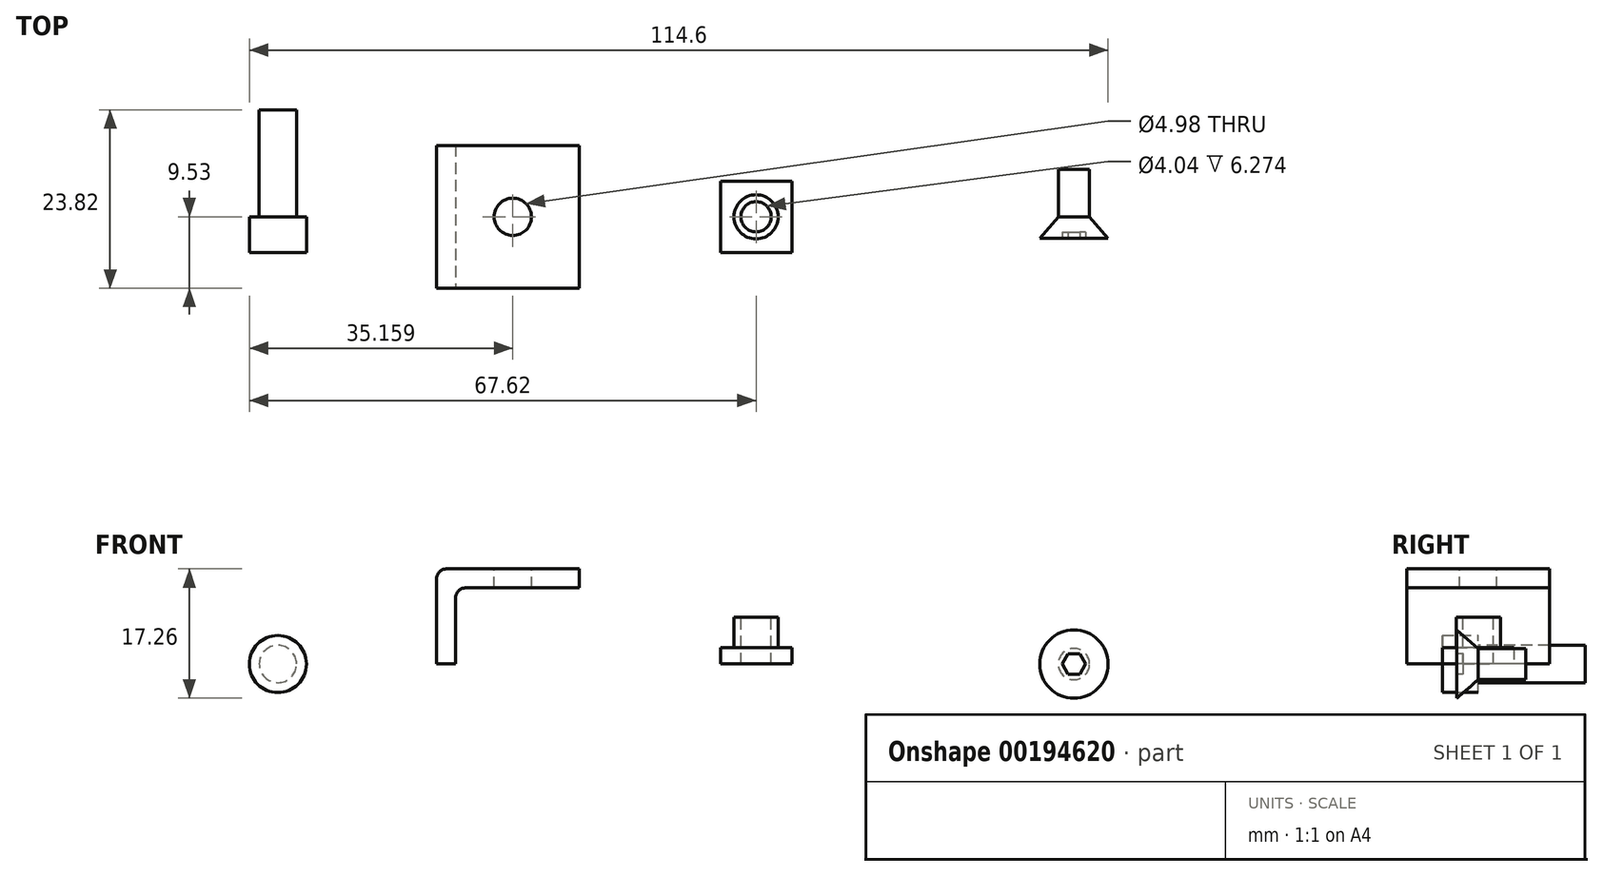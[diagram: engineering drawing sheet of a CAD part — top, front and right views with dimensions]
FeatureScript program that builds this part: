
annotation { "Feature Type Name" : "Feature", "Feature Type Description" : "" }
export const myFeature = defineFeature(function(context is Context, id is Id, definition is map)
    precondition{}
    {
        {
            var Q0;
            Q0=qCreatedBy(makeId("Top.planeOp"),FACE);
            var sketch = newSketch(context, id + "F0", { "sketchPlane" : qUnion([Q0])});
            skLineSegment(sketch, "E0.bottom", {"start": v(4.76, 4.76) * mm, "end": v(-4.76, 4.76) * mm});
            skLineSegment(sketch, "E0.top", {"start": v(4.76, -4.76) * mm, "end": v(-4.76, -4.76) * mm});
            skLineSegment(sketch, "E0.left", {"start": v(4.76, 4.76) * mm, "end": v(4.76, -4.76) * mm});
            skLineSegment(sketch, "E0.right", {"start": v(-4.76, 4.76) * mm, "end": v(-4.76, -4.76) * mm});
            skPoint(sketch, "E0.middle", {"position": v(0, 0) * mm});
            skSolve(sketch);
        }
        {
            var Q0;
            Q0=qSketchRegion(id+"F0",true);
            extrude(context, id + "F1", {"entities" : qUnion([Q0]), "depth" : 2.2 * mm});
        }
        {
            var Q0;
            Q0=makeQuery(id+"F1.opExtrude","CAP_FACE",FACE,{"disambiguationData":[OSD([sQuery(id+"F0.wireOp",EDGE,"E0.bottom"),sQuery(id+"F0.wireOp",EDGE,"E0.top"),sQuery(id+"F0.wireOp",EDGE,"E0.left"),sQuery(id+"F0.wireOp",EDGE,"E0.right")])],"isStart":false});
            var sketch = newSketch(context, id + "F2", { "sketchPlane" : qUnion([Q0])});
            skCircle(sketch, "E1", {"center": v(0, 0) * mm, "radius": 2.95 * mm});
            skSolve(sketch);
        }
        {
            var Q0;
            Q0=qSketchRegion(id+"F2",true);
            extrude(context, id + "F3", {"entities" : qUnion([Q0]), "operationType" : NewBodyOperationType.ADD, "depth" : 4.06 * mm});
        }
        {
            var Q0;
            Q0=makeQuery(id+"F3.opExtrude","CAP_FACE",FACE,{"disambiguationData":[OSD([sQuery(id+"F2.wireOp",EDGE,"E1")])],"isStart":false});
            var sketch = newSketch(context, id + "F4", { "sketchPlane" : qUnion([Q0])});
            skPoint(sketch, "E2", {"position": v(0, 0) * mm});
            skSolve(sketch);
        }
        {
            var Q0;
            Q0=sQuery(id+"F4.wireOp",VERTEX,"E2");
            var Q1;
            Q1=makeQuery(id+"F1.opExtrude","SWEPT_BODY",BODY,{"disambiguationData":[OSD([sQuery(id+"F0.wireOp",EDGE,"E0.bottom"),sQuery(id+"F0.wireOp",EDGE,"E0.top"),sQuery(id+"F0.wireOp",EDGE,"E0.left"),sQuery(id+"F0.wireOp",EDGE,"E0.right")])]});
            hole(context, id + "F5", {"style" : HoleStyle.SIMPLE, "holeDiameter" : 4.04 * mm, "endStyle" : HoleEndStyle.THROUGH, "locations" : qUnion([Q0]), "scope" : qUnion([Q1])});
        }
        {
            var Q0;
            Q0=qCreatedBy(makeId("Front.planeOp"),FACE);
            var sketch = newSketch(context, id + "F6", { "sketchPlane" : qUnion([Q0])});
            skLineSegment(sketch, "E3.bottom", {"start": v(-42.62, 0) * mm, "end": v(-23.57, 0) * mm});
            skLineSegment(sketch, "E3.top", {"start": v(-42.62, 12.7) * mm, "end": v(-23.57, 12.7) * mm});
            skLineSegment(sketch, "E3.left", {"start": v(-42.62, 0) * mm, "end": v(-42.62, 12.7) * mm});
            skLineSegment(sketch, "E3.right", {"start": v(-23.57, 0) * mm, "end": v(-23.57, 12.7) * mm});
            skSolve(sketch);
        }
        {
            var Q0;
            Q0=qSketchRegion(id+"F6",true);
            extrude(context, id + "F7", {"entities" : qUnion([Q0]), "endBound" : BoundingType.SYMMETRIC, "depth" : 19.05 * mm});
        }
        {
            var Q0;
            Q0=makeQuery(id+"F7.opExtrude","CAP_FACE",FACE,{"disambiguationData":[OSD([sQuery(id+"F6.wireOp",EDGE,"E3.bottom"),sQuery(id+"F6.wireOp",EDGE,"E3.top"),sQuery(id+"F6.wireOp",EDGE,"E3.left"),sQuery(id+"F6.wireOp",EDGE,"E3.right")])],"isStart":false});
            var sketch = newSketch(context, id + "F8", { "sketchPlane" : qUnion([Q0])});
            skLineSegment(sketch, "E4", {"start": v(-40.08, 0) * mm, "end": v(-40.08, 10.16) * mm});
            skLineSegment(sketch, "E5", {"start": v(-40.08, 10.16) * mm, "end": v(-23.57, 10.16) * mm});
            skLineSegment(sketch, "E6", {"start": v(-23.57, 10.16) * mm, "end": v(-23.57, 0) * mm});
            skLineSegment(sketch, "E7", {"start": v(-23.57, 0) * mm, "end": v(-40.08, 0) * mm});
            skSolve(sketch);
        }
        {
            var Q0;
            Q0=qSketchRegion(id+"F8",true);
            extrude(context, id + "F9", {"entities" : qUnion([Q0]), "operationType" : NewBodyOperationType.REMOVE, "endBound" : BoundingType.THROUGH_ALL, "oppositeDirection" : true, "depth" : 25.4 * mm});
        }
        {
            var Q0;
            Q0=makeQuery(id+"F7.opExtrude","SWEPT_EDGE",EDGE,{"disambiguationData":[OSD([sQuery(id+"F6.wireOp",EDGE,"E3.top"),sQuery(id+"F6.wireOp",EDGE,"E3.left")])]});
            var Q1;
            Q1=makeQuery(id+"F9.boolean.opBoolean","COPY",EDGE,{"derivedFrom":makeQuery(id+"F9.opExtrude","SWEPT_EDGE",EDGE,{"disambiguationData":[OSD([sQuery(id+"F8.wireOp",EDGE,"E4"),sQuery(id+"F8.wireOp",EDGE,"E5")])]})});
            fillet(context, id + "F10", {"entities" : qUnion([Q0, Q1]), "radius" : 1.27 * mm, "tangentPropagation" : true, "allowEdgeOverflow" : false});
        }
        {
            var Q0;
            Q0=makeQuery(id+"F7.opExtrude","SWEPT_FACE",FACE,{"disambiguationData":[OSD([sQuery(id+"F6.wireOp",EDGE,"E3.top")])]});
            var sketch = newSketch(context, id + "F11", { "sketchPlane" : qUnion([Q0])});
            skPoint(sketch, "E8", {"position": v(-32.46, 0) * mm});
            skLineSegment(sketch, "E9", {"start": v(-32.46, 9.52) * mm, "end": v(-32.46, 0) * mm, "construction": true});
            skLineSegment(sketch, "E10", {"start": v(-32.46, -9.52) * mm, "end": v(-32.46, 0) * mm, "construction": true});
            skLineSegment(sketch, "E11", {"start": v(-32.46, 0) * mm, "end": v(-23.57, 0) * mm, "construction": true});
            skLineSegment(sketch, "E12", {"start": v(-42.62, 0) * mm, "end": v(-32.46, 0) * mm, "construction": true});
            skSolve(sketch);
        }
        {
            var Q0;
            Q0=sQuery(id+"F11.wireOp",VERTEX,"E8");
            var Q1;
            Q1=makeQuery(id+"F7.opExtrude","SWEPT_BODY",BODY,{"disambiguationData":[OSD([sQuery(id+"F6.wireOp",EDGE,"E3.bottom"),sQuery(id+"F6.wireOp",EDGE,"E3.top"),sQuery(id+"F6.wireOp",EDGE,"E3.left"),sQuery(id+"F6.wireOp",EDGE,"E3.right")])]});
            hole(context, id + "F12", {"style" : HoleStyle.SIMPLE, "holeDiameter" : 4.98 * mm, "endStyle" : HoleEndStyle.THROUGH, "locations" : qUnion([Q0]), "scope" : qUnion([Q1])});
        }
        {
            var Q0;
            Q0=qCreatedBy(makeId("Front.planeOp"),FACE);
            var sketch = newSketch(context, id + "F13", { "sketchPlane" : qUnion([Q0])});
            skCircle(sketch, "E13", {"center": v(-63.81, 0) * mm, "radius": 3.81 * mm});
            skSolve(sketch);
        }
        {
            var Q0;
            Q0=makeQuery(id+"F13.imprint","IMPRINT",FACE,{"disambiguationData":[TD([[makeQuery(id+"F13.imprint","IMPRINT",EDGE,{"derivedFrom":sQuery(id+"F13.wireOp",EDGE,"E13")}),1.0]])]});
            extrude(context, id + "F14", {"entities" : qUnion([Q0]), "depth" : 4.76 * mm});
        }
        {
            var Q0;
            Q0=makeQuery(id+"F14.opExtrude","CAP_FACE",FACE,{"disambiguationData":[OSD([sQuery(id+"F13.wireOp",EDGE,"E13")])],"isStart":true});
            var sketch = newSketch(context, id + "F15", { "sketchPlane" : qUnion([Q0])});
            skCircle(sketch, "E14", {"center": v(63.81, 0) * mm, "radius": 2.49 * mm});
            skSolve(sketch);
        }
        {
            var Q0;
            Q0=qSketchRegion(id+"F15",true);
            extrude(context, id + "F16", {"entities" : qUnion([Q0]), "operationType" : NewBodyOperationType.ADD, "depth" : 14.29 * mm});
        }
        {
            var Q0;
            Q0=qCreatedBy(makeId("Front.planeOp"),FACE);
            var sketch = newSketch(context, id + "F17", { "sketchPlane" : qUnion([Q0])});
            skCircle(sketch, "E15", {"center": v(42.42, 0) * mm, "radius": 2.08 * mm});
            skSolve(sketch);
        }
        {
            var Q0;
            Q0=makeQuery(id+"F17.imprint","IMPRINT",FACE,{"disambiguationData":[TD([[makeQuery(id+"F17.imprint","IMPRINT",EDGE,{"derivedFrom":sQuery(id+"F17.wireOp",EDGE,"E15")}),1.0]])]});
            var Q1;
            Q1=sQuery(id+"F17.wireOp",EDGE,"D0WyXGXJ-a11A-hqUu-lPQ9-7sO1lFc8ZwJV");
            extrude(context, id + "F18", {"entities" : qUnion([Q0]), "surfaceEntities" : qUnion([Q1]), "depth" : 2.84 * mm, "hasDraft" : true, "draftAngle" : 41 * degree, "hasSecondDirection" : true, "secondDirectionOppositeDirection" : true, "secondDirectionDepth" : 6.35 * mm});
        }
        {
            var Q0;
            Q0=makeQuery(id+"F18.opExtrude","CAP_FACE",FACE,{"disambiguationData":[OSD([sQuery(id+"F17.wireOp",EDGE,"E15")])],"isStart":false});
            var sketch = newSketch(context, id + "F19", { "sketchPlane" : qUnion([Q0])});
            skCircle(sketch, "E16.cCircle", {"center": v(42.42, 0) * mm, "radius": 1.34 * mm, "construction": true});
            skLineSegment(sketch, "E16.0", {"start": v(43.97, 0) * mm, "end": v(43.2, -1.34) * mm});
            skLineSegment(sketch, "E16.1", {"start": v(43.2, -1.34) * mm, "end": v(41.65, -1.34) * mm});
            skLineSegment(sketch, "E16.2", {"start": v(41.65, -1.34) * mm, "end": v(40.87, 0) * mm});
            skLineSegment(sketch, "E16.3", {"start": v(40.87, 0) * mm, "end": v(41.65, 1.34) * mm});
            skLineSegment(sketch, "E16.4", {"start": v(41.65, 1.34) * mm, "end": v(43.2, 1.34) * mm});
            skLineSegment(sketch, "E16.5", {"start": v(43.2, 1.34) * mm, "end": v(43.97, 0) * mm});
            skPoint(sketch, "E16.0.midPoint", {"position": v(43.58, -0.67) * mm});
            skSolve(sketch);
        }
        {
            var Q0;
            Q0=makeQuery(id+"F19.imprint","IMPRINT",FACE,{"disambiguationData":[TD([[makeQuery(id+"F19.imprint","IMPRINT",EDGE,{"derivedFrom":sQuery(id+"F19.wireOp",EDGE,"E16.0")}),-1.0]])]});
            extrude(context, id + "F20", {"entities" : qUnion([Q0]), "operationType" : NewBodyOperationType.REMOVE, "oppositeDirection" : true, "depth" : 0.8 * mm});
        }
    });
